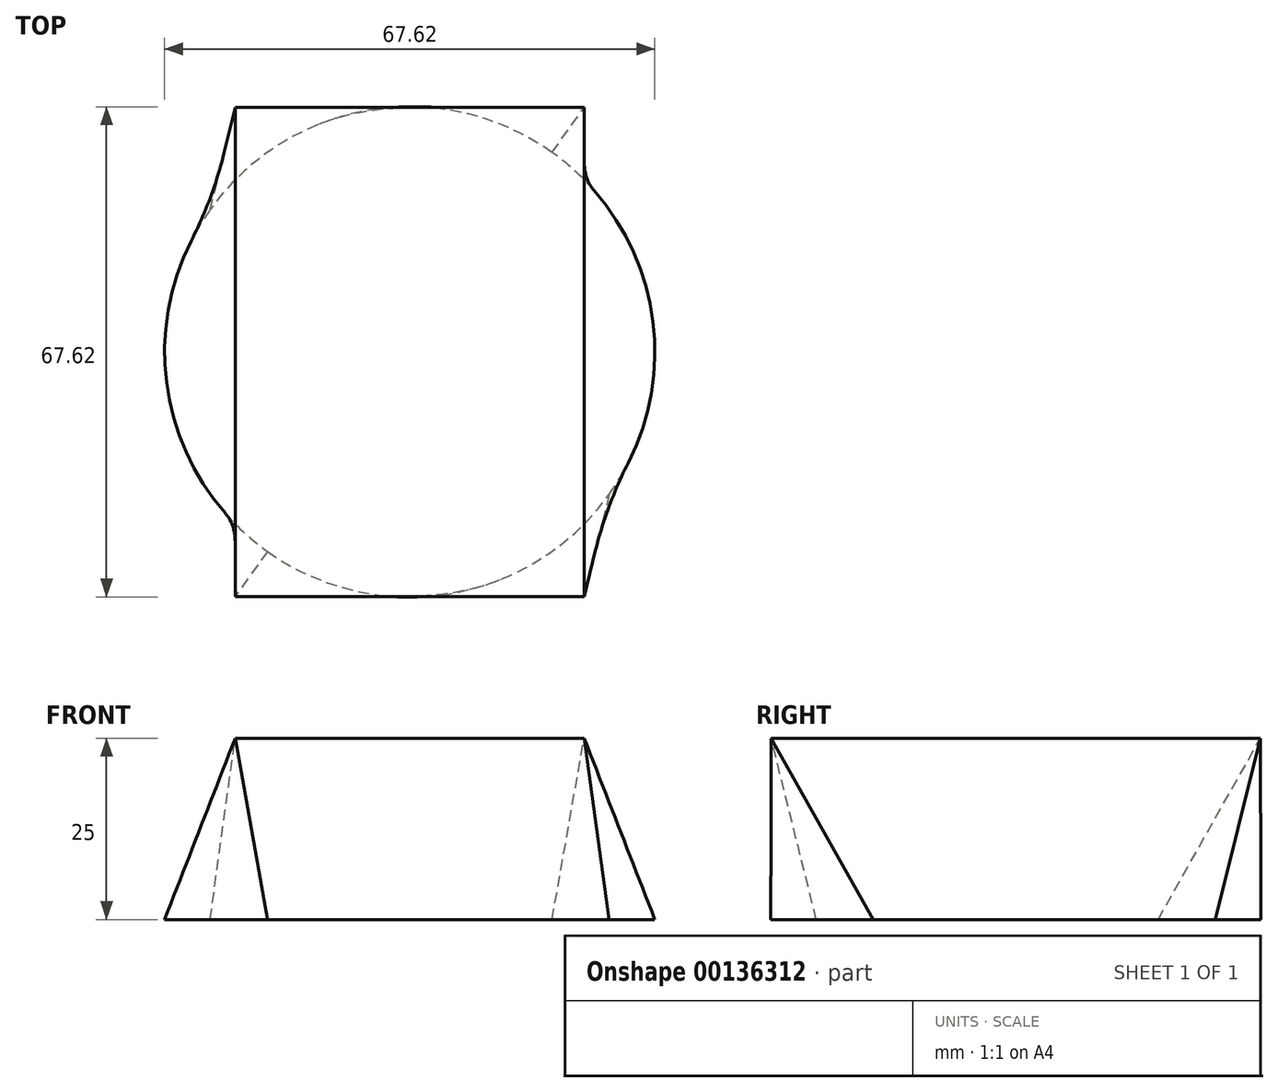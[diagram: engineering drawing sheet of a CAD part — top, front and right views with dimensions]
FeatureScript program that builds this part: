
annotation { "Feature Type Name" : "Feature", "Feature Type Description" : "" }
export const myFeature = defineFeature(function(context is Context, id is Id, definition is map)
    precondition{}
    {
        {
            var Q0;
            Q0=qCreatedBy(makeId("Top.planeOp"),FACE);
            var sketch = newSketch(context, id + "F0", { "sketchPlane" : qUnion([Q0])});
            skCircle(sketch, "E0", {"center": v(0, 0) * mm, "radius": 33.8 * mm});
            skSolve(sketch);
        }
        {
            var Q0;
            Q0=qCreatedBy(makeId("Top.planeOp"),FACE);
            cPlane(context, id + "F1", {"entities" : qUnion([Q0]), "cplaneType" : CPlaneType.OFFSET, "offset" : 25 * mm, "width" : 150 * mm, "height" : 150 * mm});
        }
        {
            var Q0;
            Q0=qCreatedBy(id+"F1.planeOp",FACE);
            var sketch = newSketch(context, id + "F2", { "sketchPlane" : qUnion([Q0])});
            skLineSegment(sketch, "E1.bottom", {"start": v(-24.08, -33.74) * mm, "end": v(24.08, -33.74) * mm});
            skLineSegment(sketch, "E1.top", {"start": v(-24.08, 33.74) * mm, "end": v(24.08, 33.74) * mm});
            skLineSegment(sketch, "E1.left", {"start": v(-24.08, -33.74) * mm, "end": v(-24.08, 33.74) * mm});
            skLineSegment(sketch, "E1.right", {"start": v(24.08, -33.74) * mm, "end": v(24.08, 33.74) * mm});
            skPoint(sketch, "E1.middle", {"position": v(0, 0) * mm});
            skSolve(sketch);
        }
        {
            var Q0;
            Q0=makeQuery(id+"F0.imprint","IMPRINT",FACE,{"disambiguationData":[TD([[makeQuery(id+"F0.imprint","IMPRINT",EDGE,{"derivedFrom":sQuery(id+"F0.wireOp",EDGE,"E0")}),1.0]])]});
            var Q1;
            Q1=makeQuery(id+"F2.imprint","IMPRINT",FACE,{"disambiguationData":[TD([[makeQuery(id+"F2.imprint","IMPRINT",EDGE,{"derivedFrom":sQuery(id+"F2.wireOp",EDGE,"E1.bottom")}),1.0]])]});
            loft(context, id + "F3", {"sheetProfilesArray" : [{ "sheetProfileEntities" : qUnion([Q0]) }, { "sheetProfileEntities" : qUnion([Q1]) }]});
        }
    });
